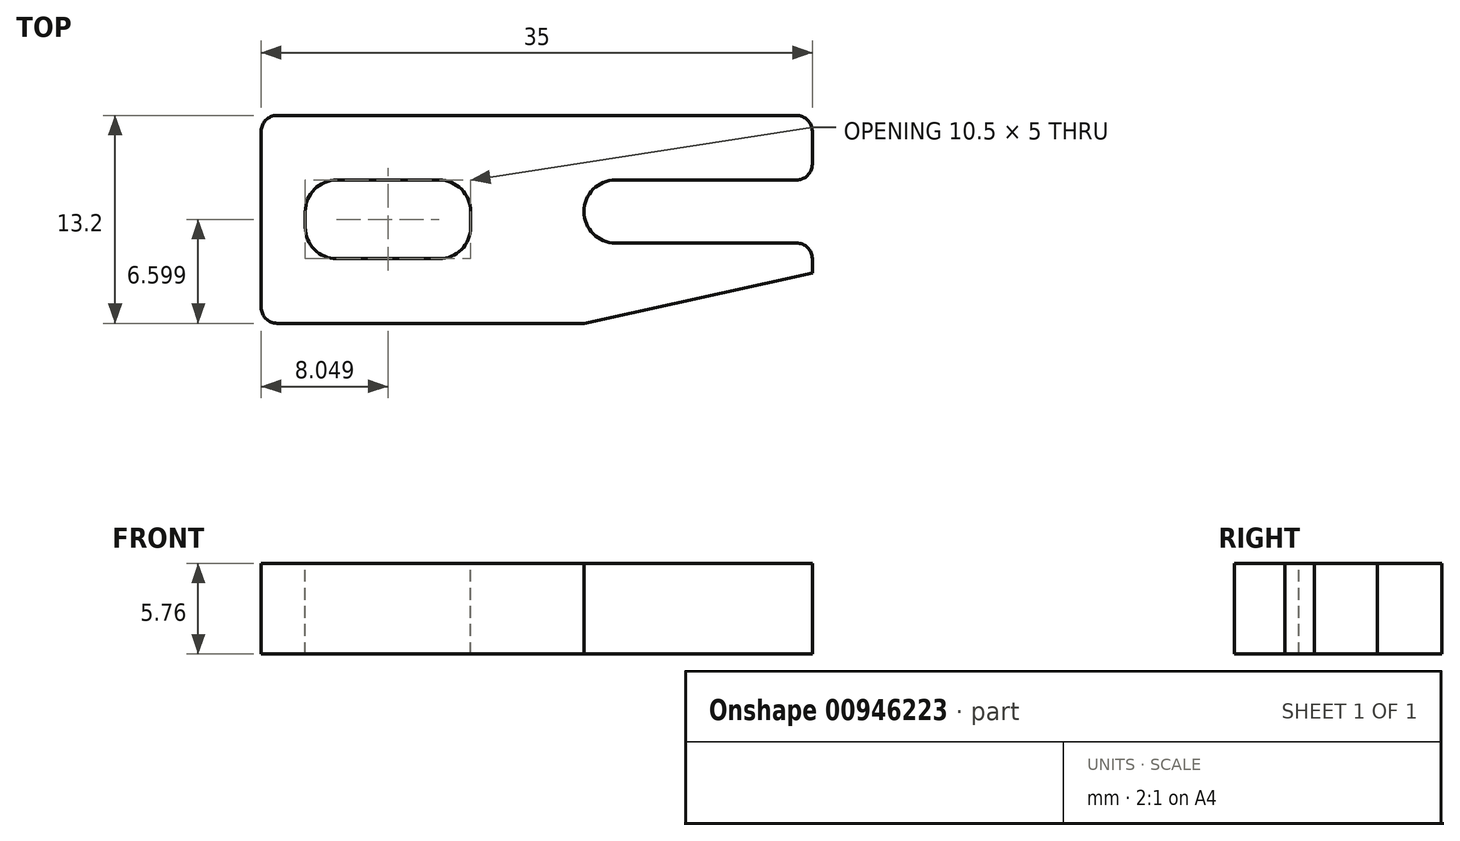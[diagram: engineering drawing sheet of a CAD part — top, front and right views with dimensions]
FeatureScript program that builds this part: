
annotation { "Feature Type Name" : "Feature", "Feature Type Description" : "" }
export const myFeature = defineFeature(function(context is Context, id is Id, definition is map)
    precondition{}
    {
        {
            var Q0;
            Q0=qCreatedBy(makeId("Top.planeOp"),FACE);
            var sketch = newSketch(context, id + "F0", { "sketchPlane" : qUnion([Q0])});
            skLineSegment(sketch, "E0.bottom", {"start": v(-25.2, 10.3) * mm, "end": v(9.8, 10.3) * mm});
            skLineSegment(sketch, "E0.top", {"start": v(-25.2, -2.9) * mm, "end": v(9.8, -2.9) * mm});
            skLineSegment(sketch, "E0.left", {"start": v(-25.2, 10.3) * mm, "end": v(-25.2, -2.9) * mm});
            skLineSegment(sketch, "E0.right", {"start": v(9.8, 10.3) * mm, "end": v(9.8, -2.9) * mm});
            skSolve(sketch);
        }
        {
            var Q0;
            Q0=makeQuery(id+"F0.imprint","IMPRINT",FACE,{"disambiguationData":[TD([[makeQuery(id+"F0.imprint","IMPRINT",EDGE,{"derivedFrom":sQuery(id+"F0.wireOp",EDGE,"E0.bottom")}),-1.0]])]});
            extrude(context, id + "F1", {"entities" : qUnion([Q0]), "depth" : 5.76 * mm, "offsetDistance" : 25 * mm});
        }
        {
            var Q0;
            Q0=makeQuery(id+"F1.opExtrude","CAP_FACE",FACE,{"disambiguationData":[OSD([sQuery(id+"F0.wireOp",EDGE,"E0.bottom"),sQuery(id+"F0.wireOp",EDGE,"E0.top"),sQuery(id+"F0.wireOp",EDGE,"E0.left"),sQuery(id+"F0.wireOp",EDGE,"E0.right")])],"isStart":false});
            var sketch = newSketch(context, id + "F2", { "sketchPlane" : qUnion([Q0])});
            skLineSegment(sketch, "E1", {"start": v(9.8, -2.9) * mm, "end": v(9.8, 0.3) * mm});
            skLineSegment(sketch, "E2", {"start": v(9.8, 0.3) * mm, "end": v(-4.7, -2.9) * mm});
            skLineSegment(sketch, "E3", {"start": v(-4.7, -2.9) * mm, "end": v(9.8, -2.9) * mm});
            skLineSegment(sketch, "E4.bottom", {"start": v(-22.4, 6.2) * mm, "end": v(-11.9, 6.2) * mm});
            skLineSegment(sketch, "E4.top", {"start": v(-22.4, 1.2) * mm, "end": v(-11.9, 1.2) * mm});
            skLineSegment(sketch, "E4.left", {"start": v(-22.4, 6.2) * mm, "end": v(-22.4, 1.2) * mm});
            skLineSegment(sketch, "E4.right", {"start": v(-11.9, 6.2) * mm, "end": v(-11.9, 1.2) * mm});
            skLineSegment(sketch, "E5.bottom", {"start": v(-4.7, 6.2) * mm, "end": v(10.3, 6.2) * mm});
            skLineSegment(sketch, "E5.top", {"start": v(-4.7, 2.2) * mm, "end": v(10.3, 2.2) * mm});
            skLineSegment(sketch, "E5.left", {"start": v(-4.7, 6.2) * mm, "end": v(-4.7, 2.2) * mm});
            skLineSegment(sketch, "E5.right", {"start": v(10.3, 6.2) * mm, "end": v(10.3, 2.2) * mm});
            skSolve(sketch);
        }
        {
            var Q0;
            Q0 = qSketchRegion(id + "F2", true);
            extrude(context, id + "F3", {"entities" : qUnion([Q0]), "operationType" : NewBodyOperationType.REMOVE, "oppositeDirection" : true, "depth" : 25 * mm, "offsetDistance" : 25 * mm});
        }
        {
            var Q0;
            Q0=makeQuery(id+"F3.boolean.opBoolean","COPY",EDGE,{"derivedFrom":makeQuery(id+"F3.opExtrude","SWEPT_EDGE",EDGE,{"disambiguationData":[OSD([sQuery(id+"F2.wireOp",EDGE,"E4.bottom"),sQuery(id+"F2.wireOp",EDGE,"E4.left")])]})});
            var Q1;
            Q1=makeQuery(id+"F3.boolean.opBoolean","COPY",EDGE,{"derivedFrom":makeQuery(id+"F3.opExtrude","SWEPT_EDGE",EDGE,{"disambiguationData":[OSD([sQuery(id+"F2.wireOp",EDGE,"E4.bottom"),sQuery(id+"F2.wireOp",EDGE,"E4.right")])]})});
            var Q2;
            Q2=makeQuery(id+"F3.boolean.opBoolean","COPY",EDGE,{"derivedFrom":makeQuery(id+"F3.opExtrude","SWEPT_EDGE",EDGE,{"disambiguationData":[OSD([sQuery(id+"F2.wireOp",EDGE,"E4.top"),sQuery(id+"F2.wireOp",EDGE,"E4.right")])]})});
            var Q3;
            Q3=makeQuery(id+"F3.boolean.opBoolean","COPY",EDGE,{"derivedFrom":makeQuery(id+"F3.opExtrude","SWEPT_EDGE",EDGE,{"disambiguationData":[OSD([sQuery(id+"F2.wireOp",EDGE,"E4.top"),sQuery(id+"F2.wireOp",EDGE,"E4.left")])]})});
            var Q4;
            Q4=makeQuery(id+"F3.boolean.opBoolean","COPY",EDGE,{"derivedFrom":makeQuery(id+"F3.opExtrude","SWEPT_EDGE",EDGE,{"disambiguationData":[OSD([sQuery(id+"F2.wireOp",EDGE,"E5.top"),sQuery(id+"F2.wireOp",EDGE,"E5.left")])]})});
            var Q5;
            Q5=makeQuery(id+"F3.boolean.opBoolean","COPY",EDGE,{"derivedFrom":makeQuery(id+"F3.opExtrude","SWEPT_EDGE",EDGE,{"disambiguationData":[OSD([sQuery(id+"F2.wireOp",EDGE,"E5.bottom"),sQuery(id+"F2.wireOp",EDGE,"E5.left")])]})});
            fillet(context, id + "F4", {"entities" : qUnion([Q0, Q1, Q2, Q3, Q4, Q5]), "radius" : 2 * mm, "tangentPropagation" : true, "allowEdgeOverflow" : false});
        }
        {
            var Q0;
            Q0=makeQuery(id+"F1.opExtrude","SWEPT_EDGE",EDGE,{"disambiguationData":[OSD([sQuery(id+"F0.wireOp",EDGE,"E0.bottom"),sQuery(id+"F0.wireOp",EDGE,"E0.right")])]});
            var Q1;
            Q1=makeQuery(id+"F3.boolean.opBoolean","INTERSECT",EDGE,{"derivedFrom":[makeQuery(id+"F1.opExtrude","SWEPT_FACE",FACE,{"disambiguationData":[OSD([sQuery(id+"F0.wireOp",EDGE,"E0.right")])]}),makeQuery(id+"F3.opExtrude","SWEPT_FACE",FACE,{"disambiguationData":[OSD([sQuery(id+"F2.wireOp",EDGE,"E5.bottom")])]})]});
            var Q2;
            Q2=makeQuery(id+"F3.boolean.opBoolean","INTERSECT",EDGE,{"derivedFrom":[makeQuery(id+"F1.opExtrude","SWEPT_FACE",FACE,{"disambiguationData":[OSD([sQuery(id+"F0.wireOp",EDGE,"E0.right")])]}),makeQuery(id+"F3.opExtrude","SWEPT_FACE",FACE,{"disambiguationData":[OSD([sQuery(id+"F2.wireOp",EDGE,"E5.top")])]})]});
            var Q3;
            Q3=makeQuery(id+"F3.boolean.opBoolean","COPY",EDGE,{"derivedFrom":makeQuery(id+"F3.opExtrude","SWEPT_EDGE",EDGE,{"disambiguationData":[OSD([sQuery(id+"F0.wireOp",EDGE,"E0.right"),sQuery(id+"F2.wireOp",EDGE,"E1"),sQuery(id+"F2.wireOp",EDGE,"E2")])]})});
            var Q4;
            Q4=makeQuery(id+"F1.opExtrude","SWEPT_EDGE",EDGE,{"disambiguationData":[OSD([sQuery(id+"F0.wireOp",EDGE,"E0.top"),sQuery(id+"F0.wireOp",EDGE,"E0.left")])]});
            var Q5;
            Q5=makeQuery(id+"F1.opExtrude","SWEPT_EDGE",EDGE,{"disambiguationData":[OSD([sQuery(id+"F0.wireOp",EDGE,"E0.bottom"),sQuery(id+"F0.wireOp",EDGE,"E0.left")])]});
            fillet(context, id + "F5", {"entities" : qUnion([Q0, Q1, Q2, Q3, Q4, Q5]), "radius" : 1 * mm, "tangentPropagation" : true, "allowEdgeOverflow" : false});
        }
    });
